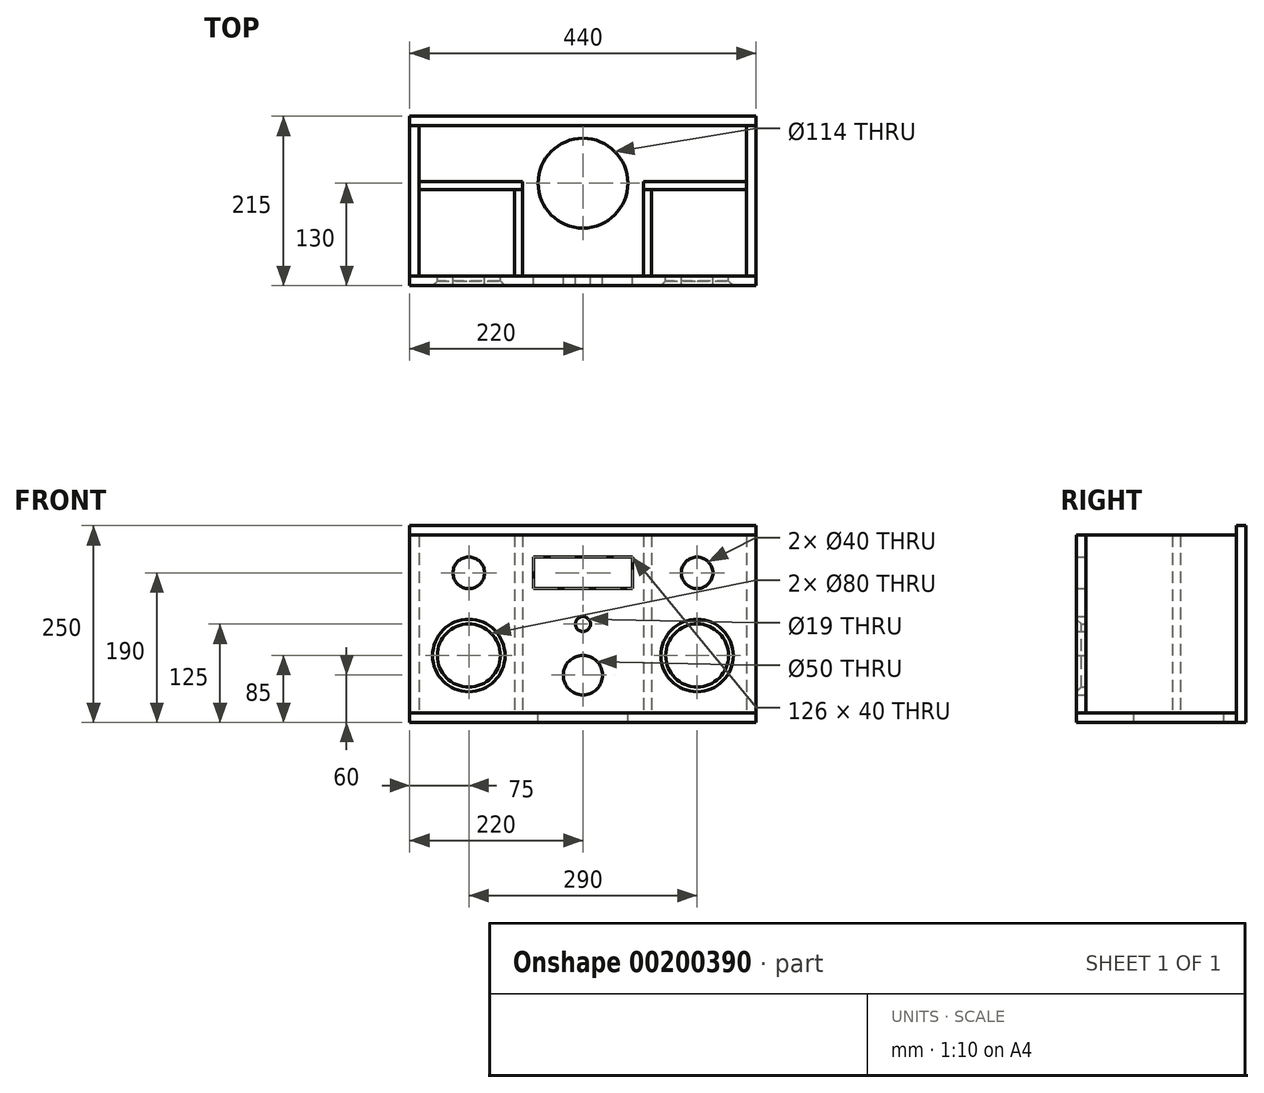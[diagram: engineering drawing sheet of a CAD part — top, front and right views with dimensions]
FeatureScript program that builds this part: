
annotation { "Feature Type Name" : "Feature", "Feature Type Description" : "" }
export const myFeature = defineFeature(function(context is Context, id is Id, definition is map)
    precondition{}
    {
        {
            var Q0;
            Q0=qCreatedBy(makeId("Front.planeOp"),FACE);
            var sketch = newSketch(context, id + "F0", { "sketchPlane" : qUnion([Q0])});
            skLineSegment(sketch, "E0.bottom", {"start": v(0, 0) * mm, "end": v(440, 0) * mm});
            skLineSegment(sketch, "E0.top", {"start": v(0, 226) * mm, "end": v(440, 226) * mm});
            skLineSegment(sketch, "E0.left", {"start": v(0, 0) * mm, "end": v(0, 226) * mm});
            skLineSegment(sketch, "E0.right", {"start": v(440, 0) * mm, "end": v(440, 226) * mm});
            skCircle(sketch, "E1", {"center": v(75, 73) * mm, "radius": 40 * mm});
            skCircle(sketch, "E2", {"center": v(75, 178) * mm, "radius": 20 * mm});
            skLineSegment(sketch, "E3", {"start": v(220, 226) * mm, "end": v(220, 0) * mm, "construction": true});
            skCircle(sketch, "E4.MirrorC", {"center": v(365, 73) * mm, "radius": 40 * mm});
            skCircle(sketch, "E5.MirrorC", {"center": v(365, 178) * mm, "radius": 20 * mm});
            skCircle(sketch, "E6", {"center": v(220, 48) * mm, "radius": 25 * mm});
            skLineSegment(sketch, "E7.bottom", {"start": v(283, 198) * mm, "end": v(157, 198) * mm});
            skLineSegment(sketch, "E7.top", {"start": v(283, 158) * mm, "end": v(157, 158) * mm});
            skLineSegment(sketch, "E7.left", {"start": v(283, 198) * mm, "end": v(283, 158) * mm});
            skLineSegment(sketch, "E7.right", {"start": v(157, 198) * mm, "end": v(157, 158) * mm});
            skPoint(sketch, "E7.middle", {"position": v(220, 178) * mm});
            skCircle(sketch, "E8", {"center": v(220, 113) * mm, "radius": 9.5 * mm});
            skLineSegment(sketch, "E9", {"start": v(220, 73) * mm, "end": v(268.92, 73) * mm, "construction": true});
            skLineSegment(sketch, "E10", {"start": v(75, 178) * mm, "end": v(365, 178) * mm, "construction": true});
            skSolve(sketch);
        }
        {
            var Q0;
            Q0=makeQuery(id+"F0.imprint","IMPRINT",FACE,{"disambiguationData":[TD([[makeQuery(id+"F0.imprint","IMPRINT",EDGE,{"derivedFrom":sQuery(id+"F0.wireOp",EDGE,"E0.bottom")}),1.0]])]});
            extrude(context, id + "F1", {"entities" : qUnion([Q0]), "depth" : 12 * mm, "offsetDistance" : 25 * mm});
        }
        {
            var Q0;
            Q0=makeQuery(id+"F1.opExtrude","CAP_FACE",FACE,{"disambiguationData":[OSD([sQuery(id+"F0.wireOp",EDGE,"E0.bottom"),sQuery(id+"F0.wireOp",EDGE,"E0.top"),sQuery(id+"F0.wireOp",EDGE,"E0.left"),sQuery(id+"F0.wireOp",EDGE,"E0.right"),sQuery(id+"F0.wireOp",EDGE,"E1"),sQuery(id+"F0.wireOp",EDGE,"E2"),sQuery(id+"F0.wireOp",EDGE,"E4.MirrorC"),sQuery(id+"F0.wireOp",EDGE,"E5.MirrorC"),sQuery(id+"F0.wireOp",EDGE,"E6"),sQuery(id+"F0.wireOp",EDGE,"E7.bottom"),sQuery(id+"F0.wireOp",EDGE,"E7.top"),sQuery(id+"F0.wireOp",EDGE,"E7.left"),sQuery(id+"F0.wireOp",EDGE,"E7.right"),sQuery(id+"F0.wireOp",EDGE,"E8")])],"isStart":true});
            var sketch = newSketch(context, id + "F2", { "sketchPlane" : qUnion([Q0])});
            skLineSegment(sketch, "E11.bottom", {"start": v(-440, 226) * mm, "end": v(-428, 226) * mm});
            skLineSegment(sketch, "E11.top", {"start": v(-440, 0) * mm, "end": v(-428, 0) * mm});
            skLineSegment(sketch, "E11.left", {"start": v(-440, 226) * mm, "end": v(-440, 0) * mm});
            skLineSegment(sketch, "E11.right", {"start": v(-428, 226) * mm, "end": v(-428, 0) * mm});
            skLineSegment(sketch, "E12.bottom", {"start": v(0, 226) * mm, "end": v(-12, 226) * mm});
            skLineSegment(sketch, "E12.top", {"start": v(0, 0) * mm, "end": v(-12, 0) * mm});
            skLineSegment(sketch, "E12.left", {"start": v(0, 226) * mm, "end": v(0, 0) * mm});
            skLineSegment(sketch, "E12.right", {"start": v(-12, 226) * mm, "end": v(-12, 0) * mm});
            skSolve(sketch);
        }
        {
            var Q0;
            Q0 = qSketchRegion(id + "F2", true);
            extrude(context, id + "F3", {"entities" : qUnion([Q0]), "depth" : 191 * mm, "offsetDistance" : 25 * mm});
        }
        {
            var Q0;
            Q0=makeQuery(id+"F1.opExtrude","CAP_FACE",FACE,{"disambiguationData":[OSD([sQuery(id+"F0.wireOp",EDGE,"E0.bottom"),sQuery(id+"F0.wireOp",EDGE,"E0.top"),sQuery(id+"F0.wireOp",EDGE,"E0.left"),sQuery(id+"F0.wireOp",EDGE,"E0.right"),sQuery(id+"F0.wireOp",EDGE,"E1"),sQuery(id+"F0.wireOp",EDGE,"E2"),sQuery(id+"F0.wireOp",EDGE,"E4.MirrorC"),sQuery(id+"F0.wireOp",EDGE,"E5.MirrorC"),sQuery(id+"F0.wireOp",EDGE,"E6"),sQuery(id+"F0.wireOp",EDGE,"E7.bottom"),sQuery(id+"F0.wireOp",EDGE,"E7.top"),sQuery(id+"F0.wireOp",EDGE,"E7.left"),sQuery(id+"F0.wireOp",EDGE,"E7.right"),sQuery(id+"F0.wireOp",EDGE,"E8")])],"isStart":true});
            var sketch = newSketch(context, id + "F4", { "sketchPlane" : qUnion([Q0])});
            skLineSegment(sketch, "E13.bottom", {"start": v(-307, 226) * mm, "end": v(-297, 226) * mm});
            skLineSegment(sketch, "E13.top", {"start": v(-307, 0) * mm, "end": v(-297, 0) * mm});
            skLineSegment(sketch, "E13.left", {"start": v(-307, 226) * mm, "end": v(-307, 0) * mm});
            skLineSegment(sketch, "E13.right", {"start": v(-297, 226) * mm, "end": v(-297, 0) * mm});
            skLineSegment(sketch, "E14.bottom", {"start": v(-133, 226) * mm, "end": v(-143, 226) * mm});
            skLineSegment(sketch, "E14.top", {"start": v(-133, 0) * mm, "end": v(-143, 0) * mm});
            skLineSegment(sketch, "E14.left", {"start": v(-133, 226) * mm, "end": v(-133, 0) * mm});
            skLineSegment(sketch, "E14.right", {"start": v(-143, 226) * mm, "end": v(-143, 0) * mm});
            skSolve(sketch);
        }
        {
            var Q0;
            Q0 = qSketchRegion(id + "F4", true);
            extrude(context, id + "F5", {"entities" : qUnion([Q0]), "depth" : 110 * mm, "offsetDistance" : 25 * mm});
        }
        {
            var Q0;
            Q0=makeQuery(id+"F5.opExtrude","SWEPT_FACE",FACE,{"disambiguationData":[OSD([sQuery(id+"F4.wireOp",EDGE,"E13.right")])]});
            var sketch = newSketch(context, id + "F6", { "sketchPlane" : qUnion([Q0])});
            skLineSegment(sketch, "E15.bottom", {"start": v(-110, 226) * mm, "end": v(-120, 226) * mm});
            skLineSegment(sketch, "E15.top", {"start": v(-110, 0) * mm, "end": v(-120, 0) * mm});
            skLineSegment(sketch, "E15.left", {"start": v(-110, 226) * mm, "end": v(-110, 0) * mm});
            skLineSegment(sketch, "E15.right", {"start": v(-120, 226) * mm, "end": v(-120, 0) * mm});
            skSolve(sketch);
        }
        {
            var Q0;
            Q0 = qSketchRegion(id + "F6", true);
            extrude(context, id + "F7", {"entities" : qUnion([Q0]), "endBound" : BoundingType.UP_TO_NEXT, "oppositeDirection" : true, "depth" : 25 * mm, "offsetDistance" : 25 * mm});
        }
        {
            var Q0;
            Q0=makeQuery(id+"F5.opExtrude","SWEPT_FACE",FACE,{"disambiguationData":[OSD([sQuery(id+"F4.wireOp",EDGE,"E14.right")])]});
            var sketch = newSketch(context, id + "F8", { "sketchPlane" : qUnion([Q0])});
            skLineSegment(sketch, "E16.bottom", {"start": v(110, 226) * mm, "end": v(120, 226) * mm});
            skLineSegment(sketch, "E16.top", {"start": v(110, 0) * mm, "end": v(120, 0) * mm});
            skLineSegment(sketch, "E16.left", {"start": v(110, 226) * mm, "end": v(110, 0) * mm});
            skLineSegment(sketch, "E16.right", {"start": v(120, 226) * mm, "end": v(120, 0) * mm});
            skSolve(sketch);
        }
        {
            var Q0;
            Q0 = qSketchRegion(id + "F8", true);
            extrude(context, id + "F9", {"entities" : qUnion([Q0]), "endBound" : BoundingType.UP_TO_NEXT, "oppositeDirection" : true, "depth" : 25 * mm, "offsetDistance" : 25 * mm});
        }
        {
            var Q0;
            Q0=makeQuery(id+"F1.opExtrude","SWEPT_FACE",FACE,{"disambiguationData":[OSD([sQuery(id+"F0.wireOp",EDGE,"E0.right")])]});
            var sketch = newSketch(context, id + "F10", { "sketchPlane" : qUnion([Q0])});
            skPoint(sketch, "E17.0", {"position": v(191, 0) * mm});
            skLineSegment(sketch, "E18.bottom", {"start": v(-12, 0) * mm, "end": v(191, 0) * mm});
            skLineSegment(sketch, "E18.top", {"start": v(-12, -12) * mm, "end": v(191, -12) * mm});
            skLineSegment(sketch, "E18.left", {"start": v(-12, 0) * mm, "end": v(-12, -12) * mm});
            skLineSegment(sketch, "E18.right", {"start": v(191, 0) * mm, "end": v(191, -12) * mm});
            skSolve(sketch);
        }
        {
            var Q0;
            Q0 = qSketchRegion(id + "F10", true);
            extrude(context, id + "F11", {"entities" : qUnion([Q0]), "oppositeDirection" : true, "depth" : 440 * mm, "offsetDistance" : 25 * mm});
        }
        {
            var Q0;
            Q0=makeQuery(id+"F11.opExtrude","SWEPT_FACE",FACE,{"disambiguationData":[OSD([sQuery(id+"F10.wireOp",EDGE,"E18.right")])]});
            var sketch = newSketch(context, id + "F12", { "sketchPlane" : qUnion([Q0])});
            skLineSegment(sketch, "E19.bottom", {"start": v(-440, -12) * mm, "end": v(0, -12) * mm});
            skLineSegment(sketch, "E19.top", {"start": v(-440, 238) * mm, "end": v(0, 238) * mm});
            skLineSegment(sketch, "E19.left", {"start": v(-440, -12) * mm, "end": v(-440, 238) * mm});
            skLineSegment(sketch, "E19.right", {"start": v(0, -12) * mm, "end": v(0, 238) * mm});
            skSolve(sketch);
        }
        {
            var Q0;
            Q0 = qSketchRegion(id + "F12", true);
            extrude(context, id + "F13", {"entities" : qUnion([Q0]), "depth" : 12 * mm, "offsetDistance" : 25 * mm});
        }
        {
            var Q0;
            Q0=makeQuery(id+"F11.opExtrude","SWEPT_FACE",FACE,{"disambiguationData":[OSD([sQuery(id+"F10.wireOp",EDGE,"E18.bottom")])]});
            var sketch = newSketch(context, id + "F14", { "sketchPlane" : qUnion([Q0])});
            skCircle(sketch, "E20", {"center": v(220, 118) * mm, "radius": 57 * mm});
            skPoint(sketch, "E20.centerSnap0", {"position": v(220, 191) * mm});
            skSolve(sketch);
        }
        {
            var Q0;
            Q0 = qSketchRegion(id + "F14", true);
            extrude(context, id + "F15", {"entities" : qUnion([Q0]), "operationType" : NewBodyOperationType.REMOVE, "oppositeDirection" : true, "depth" : 12 * mm, "offsetDistance" : 25 * mm});
        }
        {
            var Q0;
            Q0=makeQuery(id+"F1.opExtrude","CAP_EDGE",EDGE,{"disambiguationData":[OSD([sQuery(id+"F0.wireOp",EDGE,"E4.MirrorC")])],"isStart":false});
            var Q1;
            Q1=makeQuery(id+"F1.opExtrude","CAP_EDGE",EDGE,{"disambiguationData":[OSD([sQuery(id+"F0.wireOp",EDGE,"E1")])],"isStart":false});
            chamfer(context, id + "F16", {"entities" : qUnion([Q0, Q1]), "width" : 6 * mm, "tangentPropagation" : true});
        }
    });
